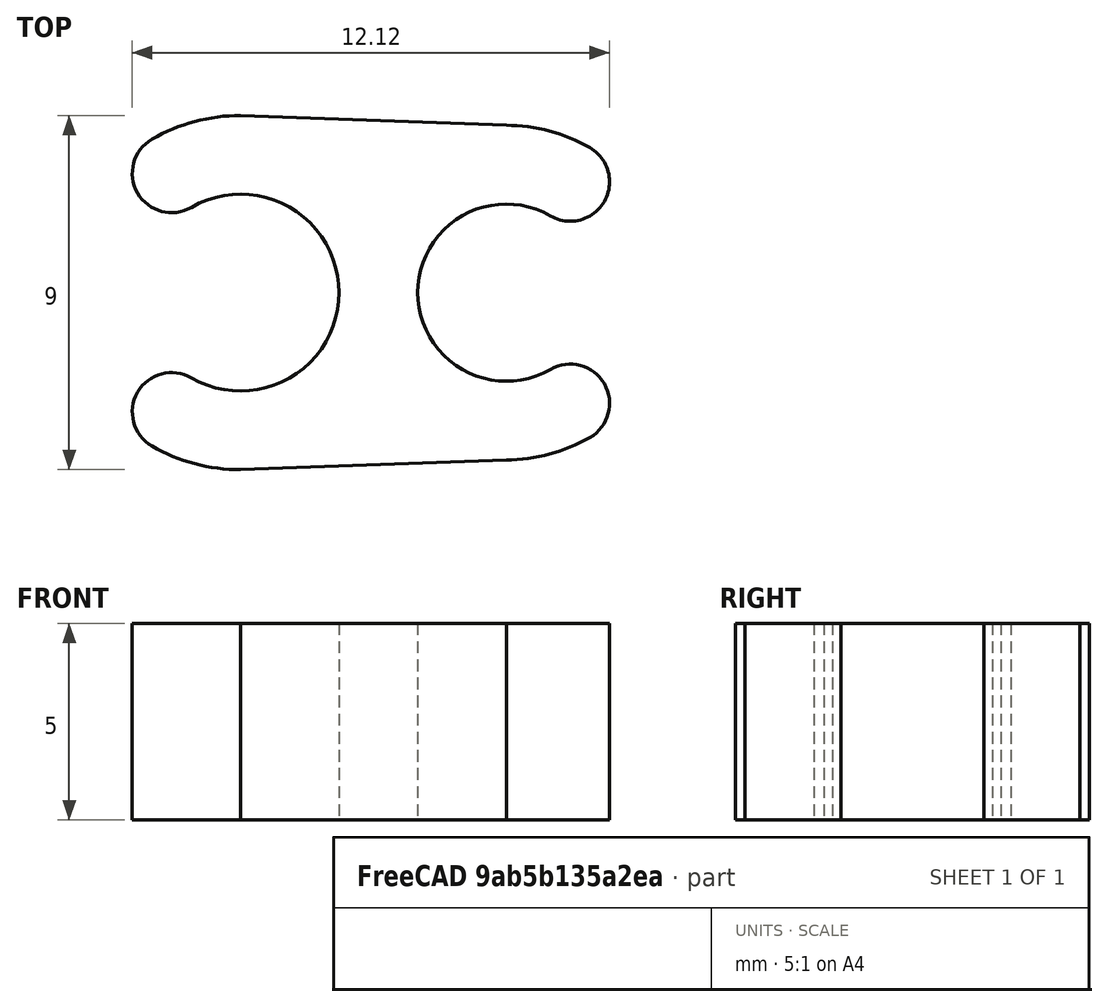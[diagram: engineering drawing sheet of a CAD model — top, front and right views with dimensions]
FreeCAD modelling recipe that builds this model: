
FCSTD DOCUMENT  (FreeCAD 0.20RUnknown)
Label: CableClip
License: All rights reserved
LicenseURL: http://en.wikipedia.org/wiki/All_rights_reserved
objects: Sketcher::SketchObject×1, PartDesign::Pad×1, PartDesign::Body×1
note: 4 computed .brp shape members not serialized (recipe doc carries the construction recipe); baked Part::Feature solids carry a one-line shape summary decoded from their .brp

FEATURE [Sketcher::SketchObject] Sketch001  label="Sketch"
  FullyConstrained = true
  MapMode = 5
  Support = -> [XY_Plane]
  sketch-geometry (34):
    g0: GeomPoint X=-3.5 Y=4.5 Z=0
    g1: GeomPoint X=-3.5 Y=-4.5 Z=0
    g2: GeomPoint X=3.25 Y=4.25 Z=0
    g3: GeomPoint X=3.25 Y=-4.25 Z=0
    g4: GeomPoint X=3.25 Y=2.25 Z=0
    g5: GeomPoint X=3.25 Y=-2.25 Z=0
    g6: GeomPoint X=-3.5 Y=-2.5 Z=0
    g7: GeomPoint X=-3.5 Y=2.5 Z=0
    g8: LineSegment StartX=-3.5 StartY=4.5 StartZ=0 EndX=3.25 EndY=4.25 EndZ=0
    g9: LineSegment StartX=-3.5 StartY=-4.5 StartZ=0 EndX=3.25 EndY=-4.25 EndZ=0
    g10: LineSegment StartX=-3.5 StartY=2.5 StartZ=0 EndX=-3.5 EndY=4.5 EndZ=0
    g11: LineSegment StartX=-3.5 StartY=-2.5 StartZ=0 EndX=-3.5 EndY=-4.5 EndZ=0
    g12: LineSegment StartX=3.25 StartY=2.25 StartZ=0 EndX=3.25 EndY=4.25 EndZ=0
    g13: LineSegment StartX=3.25 StartY=-2.25 StartZ=0 EndX=3.25 EndY=-4.25 EndZ=0
    g14: LineSegment StartX=-3.5 StartY=2.5 StartZ=0 EndX=-3.5 EndY=-2.5 EndZ=0
    g15: LineSegment StartX=3.25 StartY=-2.25 StartZ=0 EndX=3.25 EndY=2.25 EndZ=0
    g16: ArcOfCircle CenterX=-3.5 CenterY=0 CenterZ=0 NormalX=0 NormalY=0 NormalZ=1 AngleXU=0 Radius=4.5 StartAngle=1.5708 EndAngle=2.0944
    g17: ArcOfCircle CenterX=-3.5 CenterY=0 CenterZ=0 NormalX=0 NormalY=0 NormalZ=1 AngleXU=0 Radius=4.5 StartAngle=4.18879 EndAngle=4.71239
    g18: ArcOfCircle CenterX=-5.25 CenterY=3.03109 CenterZ=0 NormalX=0 NormalY=0 NormalZ=1 AngleXU=0 Radius=1 StartAngle=2.0944 EndAngle=5.23599
    g19: LineSegment StartX=-4.75 StartY=2.16506 StartZ=0 EndX=-5.75 EndY=3.89711 EndZ=0
    g20: ArcOfCircle CenterX=-5.25 CenterY=-3.03109 CenterZ=0 NormalX=0 NormalY=0 NormalZ=1 AngleXU=0 Radius=1 StartAngle=1.0472 EndAngle=4.18879
    g21: LineSegment StartX=-5.75 StartY=-3.89711 StartZ=0 EndX=-4.75 EndY=-2.16506 EndZ=0
    g22: ArcOfCircle CenterX=3.25 CenterY=0 CenterZ=0 NormalX=0 NormalY=0 NormalZ=1 AngleXU=0 Radius=4.25 StartAngle=1.0472 EndAngle=1.5708
    g23: ArcOfCircle CenterX=3.25 CenterY=0 CenterZ=0 NormalX=0 NormalY=0 NormalZ=1 AngleXU=0 Radius=4.25 StartAngle=4.71239 EndAngle=5.23599
    g24: ArcOfCircle CenterX=4.875 CenterY=2.81458 CenterZ=0 NormalX=0 NormalY=0 NormalZ=1 AngleXU=0 Radius=1 StartAngle=4.18879 EndAngle=7.33038
    g25: ArcOfCircle CenterX=4.875 CenterY=-2.81458 CenterZ=0 NormalX=0 NormalY=0 NormalZ=1 AngleXU=0 Radius=1 StartAngle=5.23599 EndAngle=8.37758
    g26: LineSegment StartX=5.375 StartY=-3.68061 StartZ=0 EndX=4.375 EndY=-1.94856 EndZ=0
    g27: LineSegment StartX=4.375 StartY=1.94856 StartZ=0 EndX=5.375 EndY=3.68061 EndZ=0
    g28: Circle CenterX=-3.5 CenterY=0 CenterZ=0 NormalX=0 NormalY=0 NormalZ=1 AngleXU=0 Radius=2.5
    g29: Circle CenterX=3.25 CenterY=0 CenterZ=0 NormalX=0 NormalY=0 NormalZ=1 AngleXU=0 Radius=2.25
    g30: GeomPoint X=-1 Y=0 Z=0
    g31: GeomPoint X=1 Y=0 Z=0
    g32: ArcOfCircle CenterX=-3.5 CenterY=0 CenterZ=0 NormalX=0 NormalY=0 NormalZ=1 AngleXU=0 Radius=2.5 StartAngle=4.18879 EndAngle=8.37758
    g33: ArcOfCircle CenterX=3.25 CenterY=0 CenterZ=0 NormalX=0 NormalY=0 NormalZ=1 AngleXU=0 Radius=2.25 StartAngle=1.0472 EndAngle=5.23599
  constraints (81):
    c: Coincident(g8,g0)
    c: Coincident(g8,g2)
    c: Coincident(g9,g1)
    c: Coincident(g9,g3)
    c: Coincident(g10,g7)
    c: Coincident(g10,g8)
    c: Vertical(g10)
    c: Coincident(g11,g6)
    c: Coincident(g11,g9)
    c: Vertical(g11)
    c: Coincident(g12,g4)
    c: Coincident(g12,g8)
    c: Vertical(g12)
    c: Coincident(g13,g5)
    c: Coincident(g13,g9)
    c: Vertical(g13)
    c: Coincident(g14,g7)
    c: Coincident(g14,g6)
    c: Coincident(g15,g5)
    c: Coincident(g15,g4)
    c: Vertical(g15)
    c: Vertical(g14)
    c: Equal(g12,g13)
    c: Equal(g13,g11)
    c: Equal(g11,g10)
    c: Distance(g10) = 2
    c: Coincident(g16,g8)
    c: Coincident(g17,g16)
    c: Coincident(g17,g9)
    c: Angle(g17) = 0.523599
    c: Angle(g16) = 0.523599
    c: Coincident(g18,g16)
    c: Coincident(g19,g18)
    c: Coincident(g19,g16)
    c: PointOnObject(g18,g19)
    c: Coincident(g20,g17)
    c: Coincident(g21,g17)
    c: Coincident(g21,g20)
    c: PointOnObject(g20,g21)
    c: Coincident(g22,g8)
    c: Coincident(g23,g22)
    c: Coincident(g23,g9)
    c: Coincident(g24,g22)
    c: Coincident(g25,g23)
    c: Coincident(g26,g23)
    c: Coincident(g26,g25)
    c: Coincident(g27,g24)
    c: Coincident(g27,g22)
    c: PointOnObject(g24,g27)
    c: PointOnObject(g25,g26)
    c: Coincident(g28,g16)
    c: PointOnObject(g7,g28)
    c: Radius(g28) = 2.5
    c: Coincident(g29,g22)
    c: PointOnObject(g4,g29)
    c: Radius(g29) = 2.25
    c: PointOnObject(g30,g28)
    c: PointOnObject(g31,g29)
    c: PointOnObject(g30,g-1)
    c: Distance(g30,g31) = 2
    c: PointOnObject(g24,g29)
    c: PointOnObject(g20,g28)
    c: PointOnObject(g5,g29)
    c: PointOnObject(g6,g28)
    c: Coincident(g32,g16)
    c: Coincident(g32,g18)
    c: Coincident(g32,g20)
    c: Coincident(g33,g22)
    c: Coincident(g33,g25)
    c: Coincident(g33,g24)
    c: PointOnObject(g22,g-1)
    c: PointOnObject(g16,g-1)
    c: Symmetric(g31,g30,g-2)
    c: Perpendicular(g28,g19)
    c: Perpendicular(g28,g21)
    c: Perpendicular(g29,g26)
    c: Perpendicular(g29,g27)
    c: PointOnObject(g16,g14)
    c: PointOnObject(g22,g15)
    c: Angle(g22) = 0.523599
    c: Angle(g23) = 0.523599
FEATURE [PartDesign::Pad] Pad
  Direction = (0,0,1)
  Length = 5
  Length2 = 10
  Profile = -> Sketch001
  ReferenceAxis = -> Sketch001 [N_Axis]
  Type = 0
FEATURE [PartDesign::Body] Body
  Group = -> [Sketch001,Pad]
  Origin = -> Origin
  Tip = -> Pad
